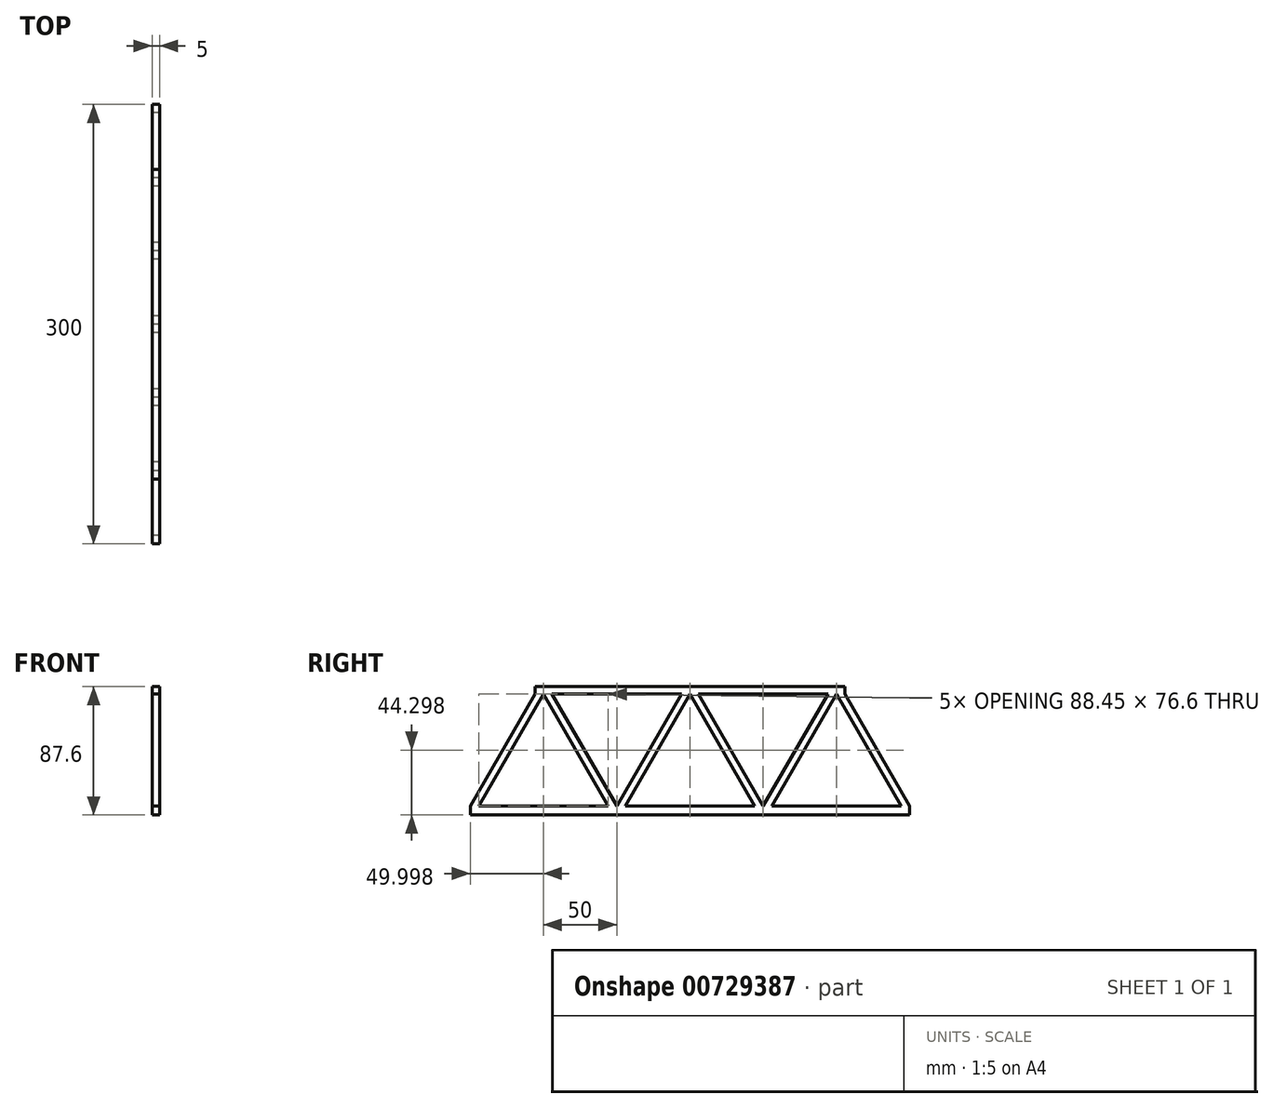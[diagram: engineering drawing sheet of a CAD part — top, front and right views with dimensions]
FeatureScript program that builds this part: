
annotation { "Feature Type Name" : "Feature", "Feature Type Description" : "" }
export const myFeature = defineFeature(function(context is Context, id is Id, definition is map)
    precondition{}
    {
        {
            var Q0;
            Q0=qCreatedBy(makeId("Right.planeOp"),FACE);
            var sketch = newSketch(context, id + "F0", { "sketchPlane" : qUnion([Q0])});
            skLineSegment(sketch, "E0.bottom", {"start": v(183.55, -42.6) * mm, "end": v(-116.45, -42.6) * mm});
            skLineSegment(sketch, "E0.top", {"start": v(183.55, -36.6) * mm, "end": v(-116.45, -36.6) * mm});
            skLineSegment(sketch, "E0.left", {"start": v(183.55, -42.6) * mm, "end": v(183.55, -36.6) * mm});
            skLineSegment(sketch, "E0.right", {"start": v(-116.45, -42.6) * mm, "end": v(-116.45, -36.6) * mm});
            skPoint(sketch, "E0.middle", {"position": v(33.55, -39.6) * mm});
            skLineSegment(sketch, "E1", {"start": v(39.32, 40) * mm, "end": v(83.55, -36.6) * mm});
            skLineSegment(sketch, "E2", {"start": v(-110.68, -36.6) * mm, "end": v(-66.45, 40) * mm});
            skLineSegment(sketch, "E3", {"start": v(-66.45, 40) * mm, "end": v(-22.23, -36.6) * mm});
            skLineSegment(sketch, "E4", {"start": v(-116.45, -36.6) * mm, "end": v(-72.23, 40) * mm});
            skLineSegment(sketch, "E5", {"start": v(-16.45, -36.6) * mm, "end": v(-60.68, 40) * mm});
            skLineSegment(sketch, "E6", {"start": v(-10.68, -36.6) * mm, "end": v(33.55, 40) * mm});
            skPoint(sketch, "E6.endSnap0", {"position": v(33.55, -36.6) * mm});
            skLineSegment(sketch, "E7", {"start": v(33.55, 40) * mm, "end": v(77.77, -36.6) * mm});
            skLineSegment(sketch, "E8", {"start": v(-16.45, -36.6) * mm, "end": v(27.77, 40) * mm});
            skLineSegment(sketch, "E9", {"start": v(89.32, -36.6) * mm, "end": v(133.55, 40) * mm});
            skLineSegment(sketch, "E10", {"start": v(133.55, 40) * mm, "end": v(177.77, -36.6) * mm});
            skLineSegment(sketch, "E11", {"start": v(83.55, -36.6) * mm, "end": v(127.77, 40) * mm});
            skLineSegment(sketch, "E12", {"start": v(183.55, -36.6) * mm, "end": v(139.32, 40) * mm});
            skLineSegment(sketch, "E13", {"start": v(-72.23, 40) * mm, "end": v(139.32, 40) * mm});
            skLineSegment(sketch, "E14", {"start": v(-72.23, 40) * mm, "end": v(-72.23, 45) * mm});
            skLineSegment(sketch, "E15", {"start": v(-72.23, 45) * mm, "end": v(139.32, 45) * mm});
            skLineSegment(sketch, "E16", {"start": v(139.32, 45) * mm, "end": v(139.32, 40) * mm});
            skSolve(sketch);
        }
        {
            var Q0;
            {var subQ0=sQuery(id+"F0.wireOp",EDGE,"E14");Q0=makeQuery(id+"F0.imprint","IMPRINT",FACE,{"disambiguationData":[TD([[makeQuery(id+"F0.imprint","IMPRINT",EDGE,{"derivedFrom":subQ0}),-1.0]])]});}
            var Q1;
            {var subQ2=sQuery(id+"F0.wireOp",EDGE,"E2");Q1=makeQuery(id+"F0.imprint","IMPRINT",FACE,{"disambiguationData":[TD([[makeQuery(id+"F0.imprint","IMPRINT",EDGE,{"derivedFrom":subQ2}),1.0]])]});}
            var Q2;
            {var subQ0=sQuery(id+"F0.wireOp",EDGE,"E3");Q2=makeQuery(id+"F0.imprint","IMPRINT",FACE,{"disambiguationData":[TD([[makeQuery(id+"F0.imprint","IMPRINT",EDGE,{"derivedFrom":subQ0}),1.0]])]});}
            var Q3;
            Q3=makeQuery(id+"F0.imprint","IMPRINT",FACE,{"disambiguationData":[TD([[makeQuery(id+"F0.imprint","IMPRINT",EDGE,{"derivedFrom":sQuery(id+"F0.wireOp",EDGE,"E0.bottom")}),-1.0]])]});
            var Q4;
            {var subQ2=sQuery(id+"F0.wireOp",EDGE,"E6");Q4=makeQuery(id+"F0.imprint","IMPRINT",FACE,{"disambiguationData":[TD([[makeQuery(id+"F0.imprint","IMPRINT",EDGE,{"derivedFrom":subQ2}),1.0]])]});}
            var Q5;
            {var subQ0=sQuery(id+"F0.wireOp",EDGE,"E1");Q5=makeQuery(id+"F0.imprint","IMPRINT",FACE,{"disambiguationData":[TD([[makeQuery(id+"F0.imprint","IMPRINT",EDGE,{"derivedFrom":subQ0}),-1.0]])]});}
            var Q6;
            {var subQ2=sQuery(id+"F0.wireOp",EDGE,"E9");Q6=makeQuery(id+"F0.imprint","IMPRINT",FACE,{"disambiguationData":[TD([[makeQuery(id+"F0.imprint","IMPRINT",EDGE,{"derivedFrom":subQ2}),1.0]])]});}
            var Q7;
            {var subQ2=sQuery(id+"F0.wireOp",EDGE,"E10");Q7=makeQuery(id+"F0.imprint","IMPRINT",FACE,{"disambiguationData":[TD([[makeQuery(id+"F0.imprint","IMPRINT",EDGE,{"derivedFrom":subQ2}),1.0]])]});}
            extrude(context, id + "F1", {"entities" : qUnion([Q0, Q1, Q2, Q3, Q4, Q5, Q6, Q7]), "depth" : 5 * mm, "offsetDistance" : 25 * mm});
        }
    });
